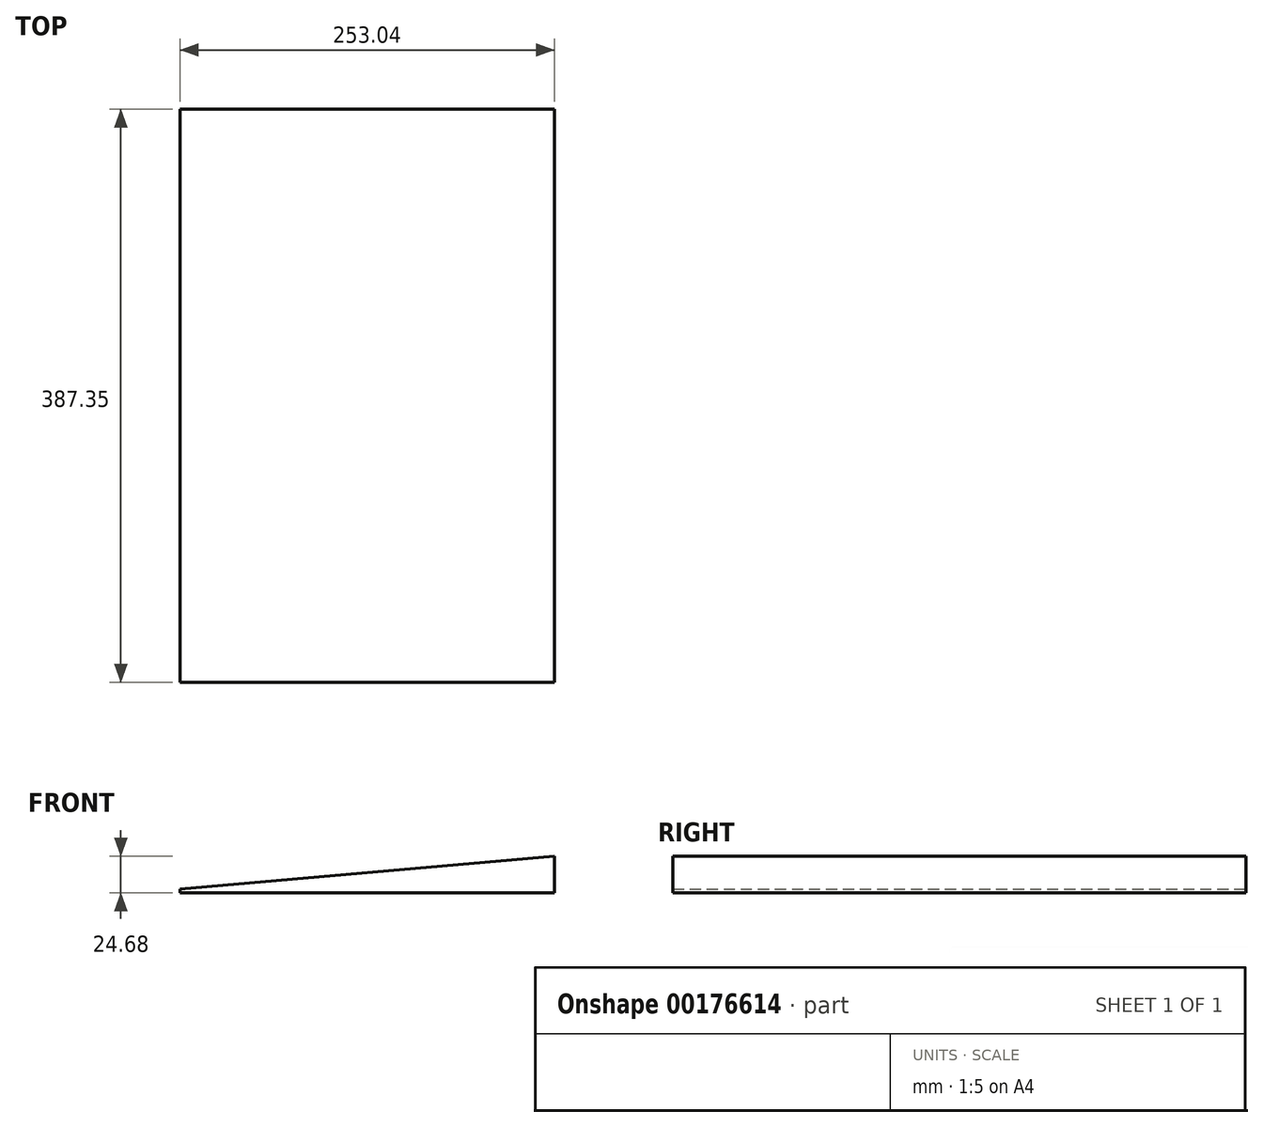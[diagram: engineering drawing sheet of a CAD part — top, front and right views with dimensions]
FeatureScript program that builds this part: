
annotation { "Feature Type Name" : "Feature", "Feature Type Description" : "" }
export const myFeature = defineFeature(function(context is Context, id is Id, definition is map)
    precondition{}
    {
        {
            var Q0;
            Q0=qCreatedBy(makeId("Front.planeOp"),FACE);
            var sketch = newSketch(context, id + "F0", { "sketchPlane" : qUnion([Q0])});
            skLineSegment(sketch, "E0", {"start": v(-117.24, 0) * mm, "end": v(135.8, 0) * mm});
            skLineSegment(sketch, "E1", {"start": v(-117.24, 0) * mm, "end": v(-117.24, 2.54) * mm});
            skLineSegment(sketch, "E2", {"start": v(-117.24, 2.54) * mm, "end": v(135.8, 24.68) * mm});
            skLineSegment(sketch, "E3", {"start": v(135.8, 24.68) * mm, "end": v(135.8, 0) * mm});
            skSolve(sketch);
        }
        {
            var Q0;
            Q0=makeQuery(id+"F0.imprint","IMPRINT",FACE,{"disambiguationData":[TD([[makeQuery(id+"F0.imprint","IMPRINT",EDGE,{"derivedFrom":sQuery(id+"F0.wireOp",EDGE,"E0")}),1.0]])]});
            extrude(context, id + "F1", {"entities" : qUnion([Q0]), "depth" : 387.35 * mm});
        }
    });
